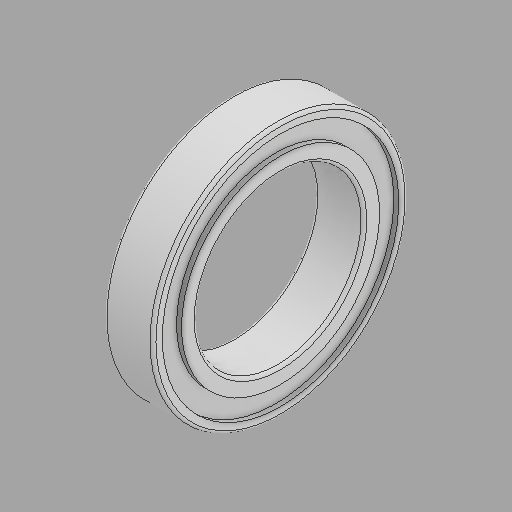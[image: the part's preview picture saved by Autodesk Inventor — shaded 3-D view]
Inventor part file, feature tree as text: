
AUTODESK INVENTOR PART (.ipt)
format: ipt  version: 2024.2 (Build 282272000, 272)  size: 163,328 bytes
history: native  units: in
note: dims shown in document units (in); Inventor stores cm internally (conversion verified against a paired STEP export)
features: fillet x1
ambient origin geometry x8: Origin, YZ Plane, XZ Plane, XY Plane, X Axis, Y Axis, Z Axis, Center Point
bodies: Solid1 (feature_tree)
feature tree (1):
  fillet  "Fillet1"  [1 undecoded]
note: 1 required parameter value undecoded (feature->parameter linkage not recoverable at this tier; creation-order binding heuristic only, values carry confidence <= 0.55)
